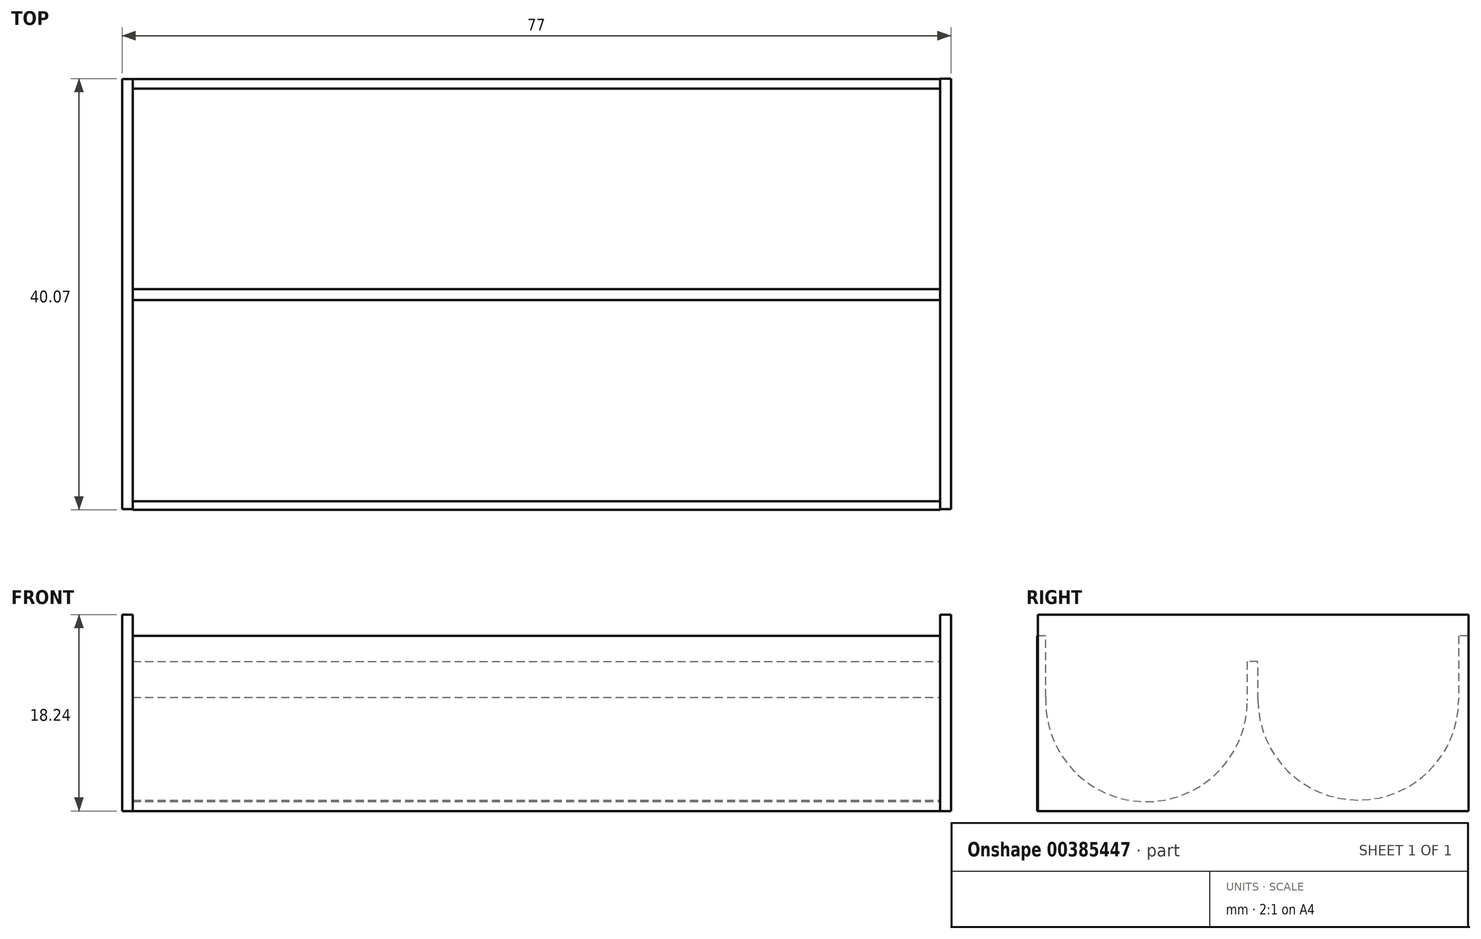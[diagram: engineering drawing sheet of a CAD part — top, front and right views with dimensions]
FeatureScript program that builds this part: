
annotation { "Feature Type Name" : "Feature", "Feature Type Description" : "" }
export const myFeature = defineFeature(function(context is Context, id is Id, definition is map)
    precondition{}
    {
        {
            var Q0;
            Q0=qCreatedBy(makeId("Right.planeOp"),FACE);
            var sketch = newSketch(context, id + "F0", { "sketchPlane" : qUnion([Q0])});
            skLineSegment(sketch, "E0.bottom", {"start": v(-18.58, 0) * mm, "end": v(21.42, 0) * mm});
            skLineSegment(sketch, "E0.top", {"start": v(-18.58, 18.24) * mm, "end": v(21.42, 18.24) * mm});
            skLineSegment(sketch, "E0.left", {"start": v(-18.58, 0) * mm, "end": v(-18.58, 18.24) * mm});
            skLineSegment(sketch, "E0.right", {"start": v(21.42, 0) * mm, "end": v(21.42, 18.24) * mm});
            skSolve(sketch);
        }
        {
            var Q0;
            Q0=makeQuery(id+"F0.imprint","IMPRINT",FACE,{"disambiguationData":[TD([[makeQuery(id+"F0.imprint","IMPRINT",EDGE,{"derivedFrom":sQuery(id+"F0.wireOp",EDGE,"E0.bottom")}),1.0]])]});
            extrude(context, id + "F1", {"entities" : qUnion([Q0]), "depth" : 1 * mm});
        }
        {
            var Q0;
            Q0=qCreatedBy(makeId("Right.planeOp"),FACE);
            var sketch = newSketch(context, id + "F2", { "sketchPlane" : qUnion([Q0])});
            skLineSegment(sketch, "E1", {"start": v(21.39, 0) * mm, "end": v(21.39, 16.28) * mm});
            skLineSegment(sketch, "E2", {"start": v(21.39, 16.28) * mm, "end": v(20.5, 16.28) * mm});
            skLineSegment(sketch, "E3", {"start": v(20.5, 16.28) * mm, "end": v(20.5, 10.33) * mm});
            skArc(sketch, "E4", {"start": v(20.5, 10.33) * mm, "mid": v(11.22, 1.01) * mm, "end": v(1.87, 10.27) * mm});
            skLineSegment(sketch, "E5", {"start": v(1.87, 10.27) * mm, "end": v(1.85, 13.89) * mm});
            skLineSegment(sketch, "E6", {"start": v(1.85, 13.89) * mm, "end": v(0.84, 13.88) * mm});
            skLineSegment(sketch, "E7", {"start": v(0.84, 13.88) * mm, "end": v(0.86, 10.27) * mm});
            skArc(sketch, "E8", {"start": v(0.86, 10.27) * mm, "mid": v(-8.64, 0.86) * mm, "end": v(-17.84, 10.56) * mm});
            skLineSegment(sketch, "E9", {"start": v(-17.84, 10.56) * mm, "end": v(-17.84, 16.28) * mm});
            skLineSegment(sketch, "E10", {"start": v(-17.84, 16.28) * mm, "end": v(-18.65, 16.28) * mm});
            skLineSegment(sketch, "E11", {"start": v(-18.65, 16.28) * mm, "end": v(-18.65, 0) * mm});
            skLineSegment(sketch, "E12", {"start": v(-18.65, 0) * mm, "end": v(21.39, 0) * mm});
            skSolve(sketch);
        }
        {
            var Q0;
            Q0=makeQuery(id+"F2.imprint","IMPRINT",FACE,{"disambiguationData":[TD([[makeQuery(id+"F2.imprint","IMPRINT",EDGE,{"derivedFrom":sQuery(id+"F2.wireOp",EDGE,"E1")}),1.0]])]});
            extrude(context, id + "F3", {"entities" : qUnion([Q0]), "operationType" : NewBodyOperationType.ADD, "oppositeDirection" : true, "depth" : 75 * mm});
        }
        {
            var Q0;
            Q0=makeQuery(id+"F3.opExtrude","CAP_FACE",FACE,{"disambiguationData":[OSD([sQuery(id+"F2.wireOp",EDGE,"E1"),sQuery(id+"F2.wireOp",EDGE,"E2"),sQuery(id+"F2.wireOp",EDGE,"E3"),sQuery(id+"F2.wireOp",EDGE,"E4"),sQuery(id+"F2.wireOp",EDGE,"E5"),sQuery(id+"F2.wireOp",EDGE,"E6"),sQuery(id+"F2.wireOp",EDGE,"E7"),sQuery(id+"F2.wireOp",EDGE,"E8"),sQuery(id+"F2.wireOp",EDGE,"E9"),sQuery(id+"F2.wireOp",EDGE,"E10"),sQuery(id+"F2.wireOp",EDGE,"E11"),sQuery(id+"F2.wireOp",EDGE,"E12")])],"isStart":false});
            var sketch = newSketch(context, id + "F4", { "sketchPlane" : qUnion([Q0])});
            skLineSegment(sketch, "E13.bottom", {"start": v(18.59, 18.24) * mm, "end": v(-21.39, 18.24) * mm});
            skLineSegment(sketch, "E13.top", {"start": v(18.59, 0) * mm, "end": v(-21.39, 0) * mm});
            skLineSegment(sketch, "E13.left", {"start": v(18.59, 18.24) * mm, "end": v(18.59, 0) * mm});
            skLineSegment(sketch, "E13.right", {"start": v(-21.39, 18.24) * mm, "end": v(-21.39, 0) * mm});
            skSolve(sketch);
        }
        {
            var Q0;
            {var subQ0=sQuery(id+"F4.wireOp",EDGE,"E13.top");Q0=makeQuery(id+"F4.imprint","IMPRINT",FACE,{"disambiguationData":[TD([[makeQuery(id+"F4.imprint","IMPRINT",EDGE,{"derivedFrom":subQ0}),-1.0]])]});}
            var Q1;
            {var subQ0=sQuery(id+"F4.wireOp",EDGE,"E13.bottom");Q1=makeQuery(id+"F4.imprint","IMPRINT",FACE,{"disambiguationData":[TD([[makeQuery(id+"F4.imprint","IMPRINT",EDGE,{"derivedFrom":subQ0}),1.0]])]});}
            extrude(context, id + "F5", {"entities" : qUnion([Q0, Q1]), "operationType" : NewBodyOperationType.ADD, "depth" : 1 * mm});
        }
    });
